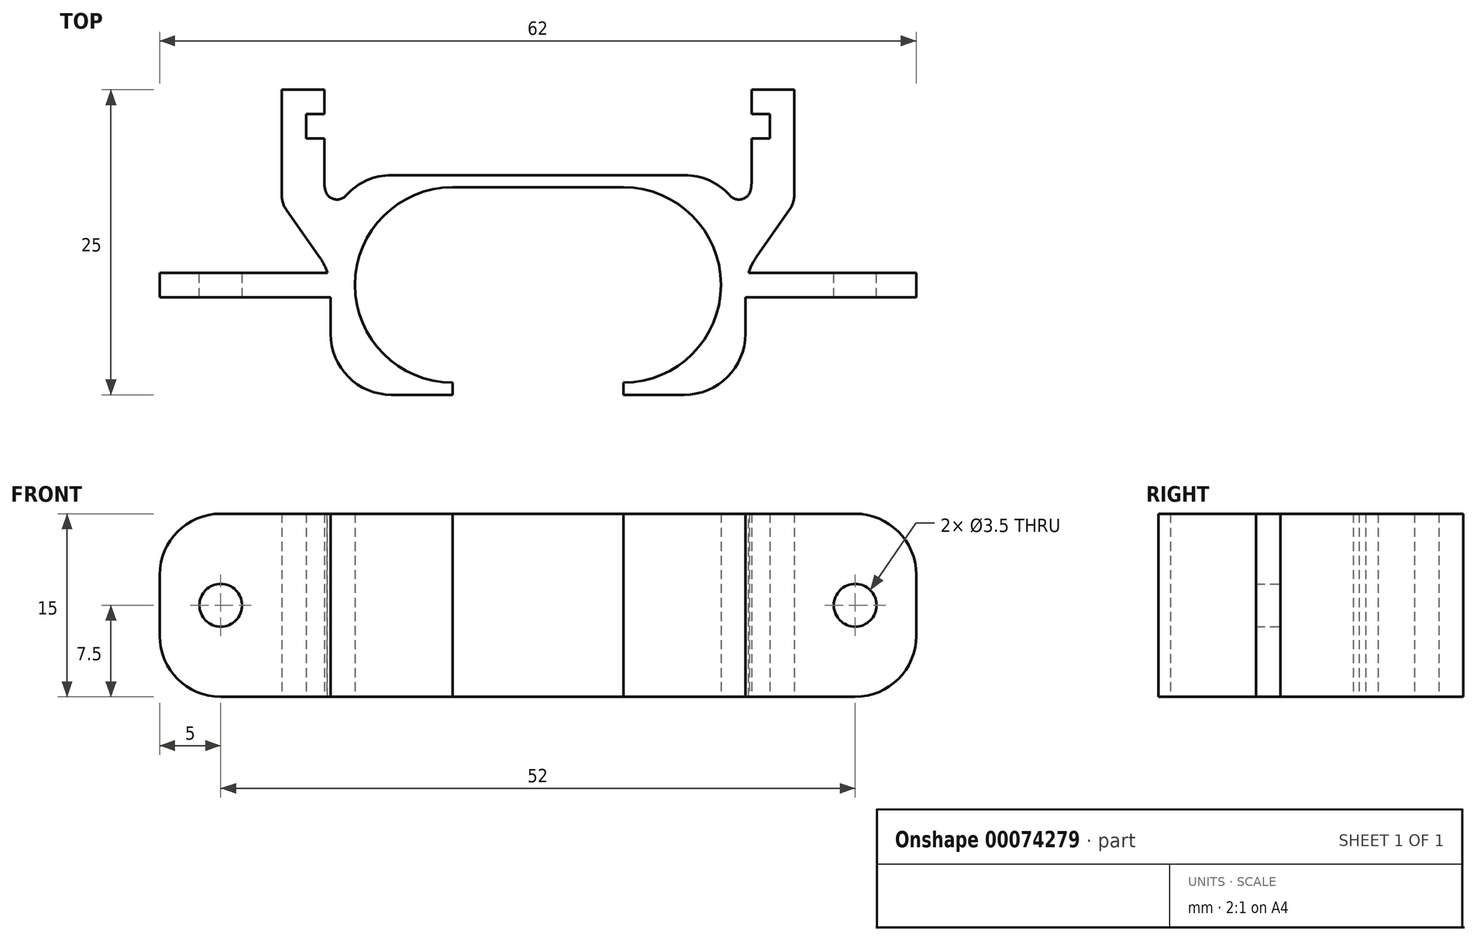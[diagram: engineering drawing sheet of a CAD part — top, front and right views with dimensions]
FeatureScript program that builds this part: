
annotation { "Feature Type Name" : "Feature", "Feature Type Description" : "" }
export const myFeature = defineFeature(function(context is Context, id is Id, definition is map)
    precondition{}
    {
        {
            var Q0;
            Q0=qCreatedBy(makeId("Top.planeOp"),FACE);
            var sketch = newSketch(context, id + "F0", { "sketchPlane" : qUnion([Q0])});
            skArc(sketch, "E0", {"start": v(-7, 8) * mm, "mid": v(-15, 0) * mm, "end": v(-7, -8) * mm});
            skArc(sketch, "E1", {"start": v(7, -8) * mm, "mid": v(15, 0) * mm, "end": v(7, 8) * mm});
            skLineSegment(sketch, "E2", {"start": v(-7, 8) * mm, "end": v(7, 8) * mm});
            skLineSegment(sketch, "E3", {"start": v(0, 0) * mm, "end": v(0, 8) * mm, "construction": true});
            skLineSegment(sketch, "E4", {"start": v(-7, 0) * mm, "end": v(-7, -8) * mm, "construction": true});
            skLineSegment(sketch, "E5", {"start": v(7, 0) * mm, "end": v(7, -8) * mm, "construction": true});
            skLineSegment(sketch, "E6", {"start": v(-7, -9) * mm, "end": v(-7, -8) * mm});
            skLineSegment(sketch, "E7", {"start": v(7, -9) * mm, "end": v(7, -8) * mm});
            skLineSegment(sketch, "E8", {"start": v(21, 7.34) * mm, "end": v(21, 16) * mm});
            skLineSegment(sketch, "E9", {"start": v(21, 16) * mm, "end": v(17.5, 16) * mm});
            skLineSegment(sketch, "E10", {"start": v(17.5, 16) * mm, "end": v(17.5, 14) * mm});
            skLineSegment(sketch, "E11", {"start": v(17.5, 14) * mm, "end": v(19, 14) * mm});
            skLineSegment(sketch, "E12", {"start": v(19, 14) * mm, "end": v(19, 12) * mm});
            skLineSegment(sketch, "E13", {"start": v(19, 12) * mm, "end": v(17.5, 12) * mm});
            skLineSegment(sketch, "E14", {"start": v(17.9, 2.3) * mm, "end": v(20.64, 6.2) * mm});
            skLineSegment(sketch, "E15", {"start": v(17.5, 12) * mm, "end": v(17.5, 8.3) * mm});
            skPoint(sketch, "E16.visualSharp", {"position": v(17.5, 8.3) * mm});
            skArc(sketch, "E16.filletArc", {"start": v(17.32, 7.47) * mm, "mid": v(17.45, 7.87) * mm, "end": v(17.5, 8.3) * mm});
            skPoint(sketch, "E17.visualSharp", {"position": v(21, 6.71) * mm});
            skArc(sketch, "E17.filletArc", {"start": v(20.64, 6.2) * mm, "mid": v(20.9, 6.74) * mm, "end": v(21, 7.34) * mm});
            skLineSegment(sketch, "E18", {"start": v(7, -9) * mm, "end": v(12, -9) * mm});
            skLineSegment(sketch, "E19", {"start": v(17, -0.58) * mm, "end": v(17, -4) * mm});
            skArc(sketch, "E20.filletArc", {"start": v(15.73, 7.33) * mm, "mid": v(14.04, 8.56) * mm, "end": v(12, 9) * mm});
            skPoint(sketch, "E21.visualSharp", {"position": v(17, -9) * mm});
            skArc(sketch, "E21.filletArc", {"start": v(12, -9) * mm, "mid": v(15.54, -7.54) * mm, "end": v(17, -4) * mm});
            skPoint(sketch, "E22.visualSharp", {"position": v(17, 1) * mm});
            skArc(sketch, "E22.filletArc", {"start": v(17.9, 2.3) * mm, "mid": v(17.23, 0.93) * mm, "end": v(17, -0.58) * mm});
            skPoint(sketch, "E23.visualSharp", {"position": v(15.73, 7.33) * mm});
            skArc(sketch, "E23.filletArc", {"start": v(15.73, 7.33) * mm, "mid": v(16.56, 7) * mm, "end": v(17.32, 7.47) * mm});
            skArc(sketch, "E24.MirrorCS", {"start": v(-17.32, 7.47) * mm, "mid": v(-17.45, 7.87) * mm, "end": v(-17.5, 8.3) * mm});
            skArc(sketch, "E25.MirrorCS", {"start": v(-20.64, 6.2) * mm, "mid": v(-20.9, 6.74) * mm, "end": v(-21, 7.34) * mm});
            skArc(sketch, "E26.MirrorCS", {"start": v(-15.73, 7.33) * mm, "mid": v(-16.56, 7) * mm, "end": v(-17.32, 7.47) * mm});
            skLineSegment(sketch, "E27.MirrorCS", {"start": v(-21, 16) * mm, "end": v(-17.5, 16) * mm});
            skPoint(sketch, "E28.MirrorP", {"position": v(-17, 1) * mm});
            skPoint(sketch, "E29.MirrorP", {"position": v(-15.73, 7.33) * mm});
            skArc(sketch, "E30.MirrorCS", {"start": v(-15.73, 7.33) * mm, "mid": v(-14.04, 8.56) * mm, "end": v(-12, 9) * mm});
            skLineSegment(sketch, "E31.MirrorCS", {"start": v(7, 8) * mm, "end": v(-7, 8) * mm});
            skLineSegment(sketch, "E32.MirrorCS", {"start": v(-17.9, 2.3) * mm, "end": v(-20.64, 6.2) * mm});
            skArc(sketch, "E33.MirrorCS", {"start": v(-7, -8) * mm, "mid": v(-15, 0) * mm, "end": v(-7, 8) * mm});
            skLineSegment(sketch, "E34.MirrorCS", {"start": v(-17.5, 16) * mm, "end": v(-17.5, 14) * mm});
            skPoint(sketch, "E35.MirrorP", {"position": v(-17.5, 8.3) * mm});
            skLineSegment(sketch, "E36.MirrorCS", {"start": v(-19, 12) * mm, "end": v(-17.5, 12) * mm});
            skLineSegment(sketch, "E37.MirrorCS", {"start": v(-19, 14) * mm, "end": v(-19, 12) * mm});
            skLineSegment(sketch, "E38.MirrorCS", {"start": v(-17.5, 12) * mm, "end": v(-17.5, 8.3) * mm});
            skLineSegment(sketch, "E39.MirrorCS", {"start": v(-17.5, 14) * mm, "end": v(-19, 14) * mm});
            skArc(sketch, "E40.MirrorCS", {"start": v(-12, -9) * mm, "mid": v(-15.54, -7.54) * mm, "end": v(-17, -4) * mm});
            skPoint(sketch, "E41.MirrorP", {"position": v(-17, -9) * mm});
            skPoint(sketch, "E42.MirrorP", {"position": v(-21, 6.71) * mm});
            skArc(sketch, "E43.MirrorCS", {"start": v(-17.9, 2.3) * mm, "mid": v(-17.23, 0.93) * mm, "end": v(-17, -0.58) * mm});
            skLineSegment(sketch, "E44.MirrorCS", {"start": v(-17, -0.58) * mm, "end": v(-17, -4) * mm});
            skLineSegment(sketch, "E45.MirrorCS", {"start": v(-7, -9) * mm, "end": v(-12, -9) * mm});
            skLineSegment(sketch, "E46.MirrorCS", {"start": v(-21, 7.34) * mm, "end": v(-21, 16) * mm});
            skLineSegment(sketch, "E47", {"start": v(-12, 9) * mm, "end": v(12, 9) * mm});
            skSolve(sketch);
        }
        {
            var Q0;
            Q0=makeQuery(id+"F0.imprint","IMPRINT",FACE,{"disambiguationData":[TD([[makeQuery(id+"F0.imprint","IMPRINT",EDGE,{"derivedFrom":sQuery(id+"F0.wireOp",EDGE,"E1")}),-1.0]])]});
            extrude(context, id + "F1", {"entities" : qUnion([Q0]), "endBound" : BoundingType.SYMMETRIC, "depth" : 15 * mm});
        }
        {
            var Q0;
            Q0=makeQuery(id+"F1.opExtrude","CAP_FACE",FACE,{"disambiguationData":[OSD([sQuery(id+"F0.wireOp",EDGE,"E1"),sQuery(id+"F0.wireOp",EDGE,"E7"),sQuery(id+"F0.wireOp",EDGE,"E8"),sQuery(id+"F0.wireOp",EDGE,"E9"),sQuery(id+"F0.wireOp",EDGE,"E10"),sQuery(id+"F0.wireOp",EDGE,"E11"),sQuery(id+"F0.wireOp",EDGE,"E12"),sQuery(id+"F0.wireOp",EDGE,"E13"),sQuery(id+"F0.wireOp",EDGE,"E14"),sQuery(id+"F0.wireOp",EDGE,"E15"),sQuery(id+"F0.wireOp",EDGE,"E16.filletArc"),sQuery(id+"F0.wireOp",EDGE,"E17.filletArc"),sQuery(id+"F0.wireOp",EDGE,"E18"),sQuery(id+"F0.wireOp",EDGE,"E19"),sQuery(id+"F0.wireOp",EDGE,"E20.filletArc"),sQuery(id+"F0.wireOp",EDGE,"E21.filletArc"),sQuery(id+"F0.wireOp",EDGE,"E22.filletArc"),sQuery(id+"F0.wireOp",EDGE,"E23.filletArc"),sQuery(id+"F0.wireOp",EDGE,"E6"),sQuery(id+"F0.wireOp",EDGE,"E24.MirrorCS"),sQuery(id+"F0.wireOp",EDGE,"E25.MirrorCS"),sQuery(id+"F0.wireOp",EDGE,"E26.MirrorCS"),sQuery(id+"F0.wireOp",EDGE,"E27.MirrorCS"),sQuery(id+"F0.wireOp",EDGE,"E30.MirrorCS"),sQuery(id+"F0.wireOp",EDGE,"E31.MirrorCS"),sQuery(id+"F0.wireOp",EDGE,"E32.MirrorCS"),sQuery(id+"F0.wireOp",EDGE,"E33.MirrorCS"),sQuery(id+"F0.wireOp",EDGE,"E34.MirrorCS"),sQuery(id+"F0.wireOp",EDGE,"E36.MirrorCS"),sQuery(id+"F0.wireOp",EDGE,"E37.MirrorCS"),sQuery(id+"F0.wireOp",EDGE,"E38.MirrorCS"),sQuery(id+"F0.wireOp",EDGE,"E39.MirrorCS"),sQuery(id+"F0.wireOp",EDGE,"E40.MirrorCS"),sQuery(id+"F0.wireOp",EDGE,"E43.MirrorCS"),sQuery(id+"F0.wireOp",EDGE,"E44.MirrorCS"),sQuery(id+"F0.wireOp",EDGE,"E45.MirrorCS"),sQuery(id+"F0.wireOp",EDGE,"E46.MirrorCS"),sQuery(id+"F0.wireOp",EDGE,"E47")])],"isStart":false});
            var sketch = newSketch(context, id + "F2", { "sketchPlane" : qUnion([Q0])});
            skLineSegment(sketch, "E48.bottom", {"start": v(16, 1) * mm, "end": v(31, 1) * mm});
            skLineSegment(sketch, "E48.top", {"start": v(16, -1) * mm, "end": v(31, -1) * mm});
            skLineSegment(sketch, "E48.left", {"start": v(16, 1) * mm, "end": v(16, -1) * mm});
            skLineSegment(sketch, "E48.right", {"start": v(31, 1) * mm, "end": v(31, -1) * mm});
            skLineSegment(sketch, "E49", {"start": v(0, 0) * mm, "end": v(41.66, 0) * mm, "construction": true});
            skLineSegment(sketch, "E50", {"start": v(0, 0) * mm, "end": v(0, 16.02) * mm, "construction": true});
            skPoint(sketch, "E50.endSnap0", {"position": v(0, 8) * mm});
            skLineSegment(sketch, "E51.MirrorCS", {"start": v(-16, 1) * mm, "end": v(-16, -1) * mm});
            skLineSegment(sketch, "E52.MirrorCS", {"start": v(-31, 1) * mm, "end": v(-31, -1) * mm});
            skLineSegment(sketch, "E53.MirrorCS", {"start": v(-16, 1) * mm, "end": v(-31, 1) * mm});
            skLineSegment(sketch, "E54.MirrorCS", {"start": v(-16, -1) * mm, "end": v(-31, -1) * mm});
            skSolve(sketch);
        }
        {
            var Q0;
            {var subQ5=sQuery(id+"F2.wireOp",EDGE,"E48.right");Q0=makeQuery(id+"F2.imprint","IMPRINT",FACE,{"disambiguationData":[TD([[makeQuery(id+"F2.imprint","IMPRINT",EDGE,{"derivedFrom":subQ5}),-1.0]])]});}
            var Q1;
            {var subQ5=sQuery(id+"F2.wireOp",EDGE,"E52.MirrorCS");Q1=makeQuery(id+"F2.imprint","IMPRINT",FACE,{"disambiguationData":[TD([[makeQuery(id+"F2.imprint","IMPRINT",EDGE,{"derivedFrom":subQ5}),1.0]])]});}
            extrude(context, id + "F3", {"entities" : qUnion([Q0, Q1]), "operationType" : NewBodyOperationType.ADD, "oppositeDirection" : true, "depth" : 15 * mm});
        }
        {
            var Q0;
            Q0=makeQuery(id+"F3.opExtrude","SWEPT_FACE",FACE,{"disambiguationData":[OSD([sQuery(id+"F2.wireOp",EDGE,"E48.bottom")])]});
            var sketch = newSketch(context, id + "F4", { "sketchPlane" : qUnion([Q0])});
            skCircle(sketch, "E55", {"center": v(-26, 0) * mm, "radius": 1.75 * mm});
            skCircle(sketch, "E56", {"center": v(26, 0) * mm, "radius": 1.75 * mm});
            skLineSegment(sketch, "E57", {"start": v(0, 0) * mm, "end": v(0, 17.4) * mm, "construction": true});
            skSolve(sketch);
        }
        {
            var Q0;
            Q0 = qSketchRegion(id + "F4", true);
            extrude(context, id + "F5", {"entities" : qUnion([Q0]), "operationType" : NewBodyOperationType.REMOVE, "oppositeDirection" : true, "depth" : 25 * mm});
        }
        {
            var Q0;
            Q0=makeQuery(id+"F3.opExtrude","CAP_EDGE",EDGE,{"disambiguationData":[OSD([sQuery(id+"F2.wireOp",EDGE,"E52.MirrorCS")])],"isStart":false});
            var Q1;
            Q1=makeQuery(id+"F3.opExtrude","CAP_EDGE",EDGE,{"disambiguationData":[OSD([sQuery(id+"F2.wireOp",EDGE,"E52.MirrorCS")])],"isStart":true});
            var Q2;
            Q2=makeQuery(id+"F3.opExtrude","CAP_EDGE",EDGE,{"disambiguationData":[OSD([sQuery(id+"F2.wireOp",EDGE,"E48.right")])],"isStart":false});
            var Q3;
            Q3=makeQuery(id+"F3.opExtrude","CAP_EDGE",EDGE,{"disambiguationData":[OSD([sQuery(id+"F2.wireOp",EDGE,"E48.right")])],"isStart":true});
            fillet(context, id + "F6", {"entities" : qUnion([Q0, Q1, Q2, Q3]), "radius" : 5 * mm, "tangentPropagation" : true, "allowEdgeOverflow" : false});
        }
    });
